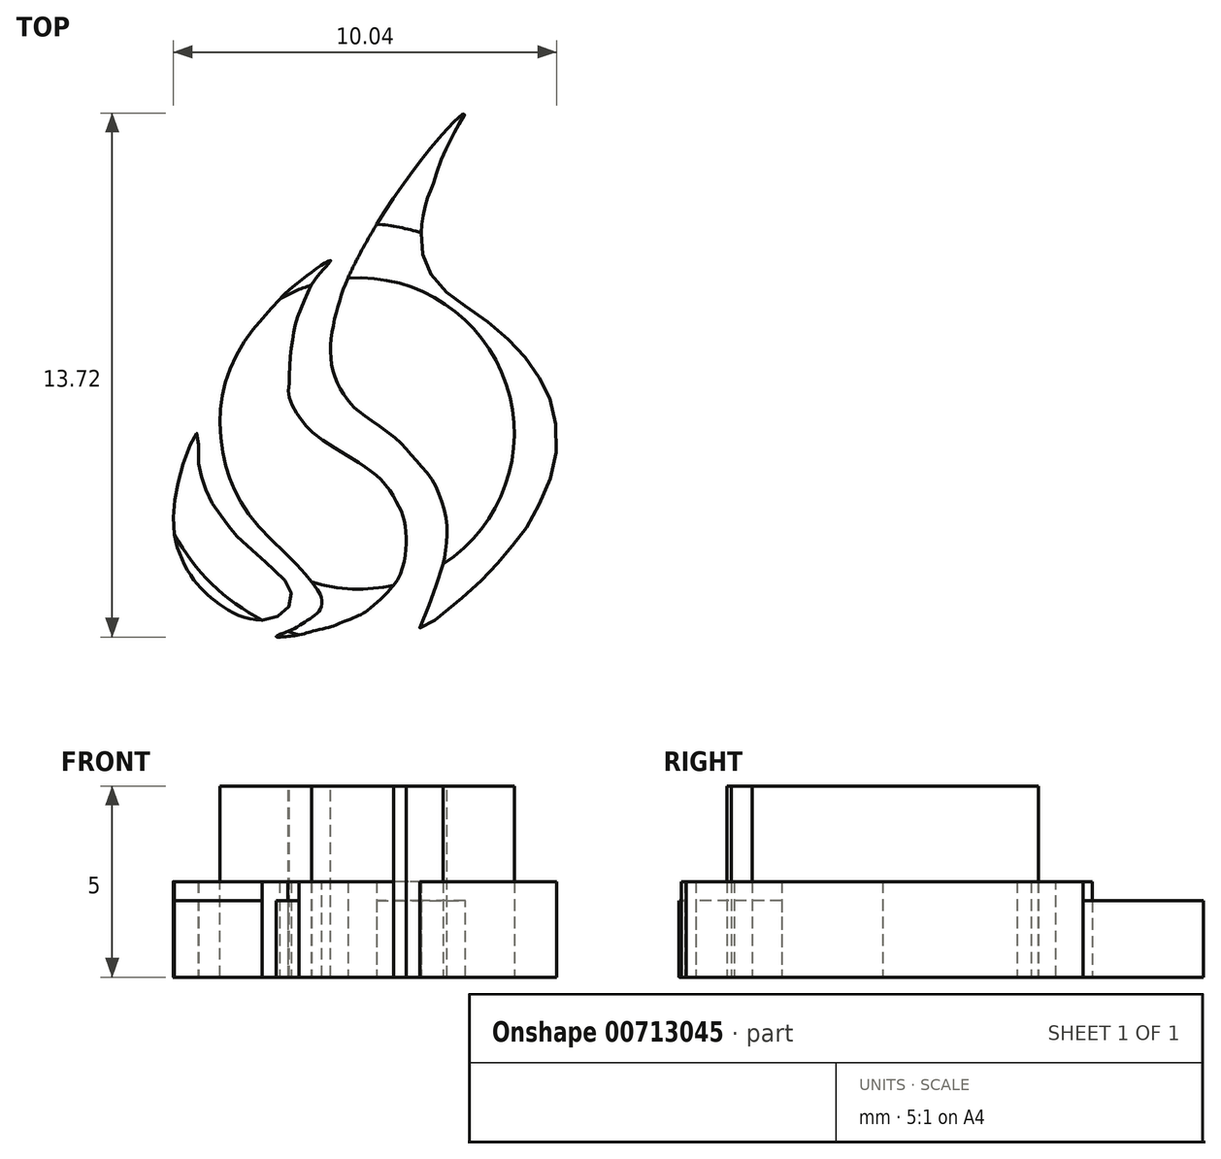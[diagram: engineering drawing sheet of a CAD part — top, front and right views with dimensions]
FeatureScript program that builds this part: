
annotation { "Feature Type Name" : "Feature", "Feature Type Description" : "" }
export const myFeature = defineFeature(function(context is Context, id is Id, definition is map)
    precondition{}
    {
        {
            var Q0;
            Q0=qCreatedBy(makeId("Top.planeOp"),FACE);
            var sketch = newSketch(context, id + "F0", { "sketchPlane" : qUnion([Q0])});
            skCircle(sketch, "E0", {"center": v(0, -0.22) * mm, "radius": 11 * mm});
            skCircle(sketch, "E1", {"center": v(0, -0.22) * mm, "radius": 5.5 * mm});
            skCircle(sketch, "E2", {"center": v(0, -0.22) * mm, "radius": 4.08 * mm});
            skLineSegment(sketch, "E3", {"start": v(0, -7.08) * mm, "end": v(0, -7.71) * mm});
            skLineSegment(sketch, "E4", {"start": v(0, 12.42) * mm, "end": v(0, -12.4) * mm});
            skFitSpline(sketch, "E5", {"points": [v(2.8, 8.17) * mm, v(2.6, 7.83) * mm, v(2.42, 7.47) * mm, v(2.19, 6.99) * mm, v(1.95, 6.3) * mm, v(1.85, 6.06) * mm, v(1.74, 5.7) * mm, v(1.66, 5.3) * mm, v(1.65, 4.93) * mm, v(1.7, 4.4) * mm, v(1.89, 3.95) * mm, v(2.3, 3.48) * mm, v(2.75, 3.15) * mm, v(3.41, 2.68) * mm, v(4, 2.17) * mm, v(4.43, 1.68) * mm, v(4.8, 1.12) * mm, v(5.05, 0.58) * mm, v(5.18, -0.22) * mm, v(5.12, -1.05) * mm, v(4.86, -1.8) * mm, v(4.5, -2.54) * mm, v(4.13, -3.03) * mm, v(3.77, -3.45) * mm, v(3.35, -3.93) * mm, v(2.94, -4.32) * mm, v(1.99, -5.12) * mm, v(1.6, -5.35) * mm, v(1.8, -4.83) * mm, v(1.94, -4.44) * mm, v(2.15, -3.86) * mm, v(2.27, -3.37) * mm, v(2.32, -2.7) * mm, v(2.17, -1.97) * mm, v(1.88, -1.37) * mm, v(1.44, -0.84) * mm, v(1, -0.37) * mm, v(0.26, 0.17) * mm, v(-0.24, 0.6) * mm, v(-0.64, 1.34) * mm, v(-0.72, 2.21) * mm, v(-0.54, 3.1) * mm, v(-0.28, 3.85) * mm, v(0.2, 4.8) * mm, v(0.8, 5.77) * mm, v(1.4, 6.62) * mm, v(2.32, 7.76) * mm, v(2.8, 8.17) * mm]});
            skFitSpline(sketch, "E6", {"points": [v(-0.73, 4.3) * mm, v(-1.1, 3.85) * mm, v(-1.34, 3.44) * mm, v(-1.52, 3.04) * mm, v(-1.66, 2.62) * mm, v(-1.72, 2.32) * mm, v(-1.77, 1.94) * mm, v(-1.8, 1.48) * mm, v(-1.82, 1.06) * mm, v(-1.83, 0.8) * mm, v(-1.7, 0.43) * mm, v(-1.47, 0.1) * mm, v(-1.17, -0.22) * mm, v(-0.24, -0.84) * mm, v(0.4, -1.26) * mm, v(0.82, -1.71) * mm, v(1.08, -2.17) * mm, v(1.2, -2.49) * mm, v(1.24, -2.93) * mm, v(1.22, -3.37) * mm, v(1.08, -3.93) * mm, v(0.8, -4.32) * mm, v(0.58, -4.55) * mm, v(0.27, -4.82) * mm, v(0, -4.99) * mm, v(-0.45, -5.17) * mm, v(-0.72, -5.28) * mm, v(-1.24, -5.4) * mm, v(-1.56, -5.5) * mm, v(-2.16, -5.54) * mm, v(-1.85, -5.4) * mm, v(-1.49, -5.21) * mm, v(-1.2, -5.02) * mm, v(-1, -4.8) * mm, v(-0.98, -4.48) * mm, v(-1.16, -4.19) * mm, v(-1.51, -3.76) * mm, v(-2.61, -2.65) * mm, v(-3.23, -1.72) * mm, v(-3.51, -0.91) * mm, v(-3.63, 0.18) * mm, v(-3.49, 1.1) * mm, v(-3.02, 2.15) * mm, v(-2.33, 3) * mm, v(-1.65, 3.68) * mm, v(-0.73, 4.3) * mm]});
            skFitSpline(sketch, "E7", {"points": [v(-4.22, -0.22) * mm, v(-4.5, -0.77) * mm, v(-4.77, -1.76) * mm, v(-4.85, -2.6) * mm, v(-4.66, -3.42) * mm, v(-4.32, -4.05) * mm, v(-3.98, -4.42) * mm, v(-3.57, -4.73) * mm, v(-3, -5.03) * mm, v(-2.28, -5.07) * mm, v(-1.8, -4.7) * mm, v(-1.84, -4.18) * mm, v(-2.25, -3.77) * mm, v(-2.53, -3.5) * mm, v(-2.85, -3.2) * mm, v(-3.24, -2.84) * mm, v(-3.52, -2.47) * mm, v(-3.87, -1.97) * mm, v(-4.1, -1.43) * mm, v(-4.2, -0.9) * mm, v(-4.22, -0.22) * mm]});
            skSolve(sketch);
        }
        {
            var Q0;
            {var subQ0=sQuery(id+"F0.wireOp",EDGE,"E5");var subQ1=sQuery(id+"F0.wireOp",EDGE,"E1");var subQ2=makeQuery(id+"F0.imprint","INTERSECT",VERTEX,{"disambiguationData":[OD(0.0)],"derivedFrom":[subQ1,subQ0]});Q0=makeQuery(id+"F0.imprint","IMPRINT",FACE,{"disambiguationData":[TD([[makeQuery(id+"F0.imprint","IMPRINT",EDGE,{"disambiguationData":[TD([[subQ2,1.0]])],"derivedFrom":subQ1}),-1.0]])]});}
            var Q1;
            {var subQ0=sQuery(id+"F0.wireOp",EDGE,"E7");var subQ1=sQuery(id+"F0.wireOp",EDGE,"E1");var subQ2=makeQuery(id+"F0.imprint","INTERSECT",VERTEX,{"disambiguationData":[OD(0.0)],"derivedFrom":[subQ1,subQ0]});Q1=makeQuery(id+"F0.imprint","IMPRINT",FACE,{"disambiguationData":[TD([[makeQuery(id+"F0.imprint","IMPRINT",EDGE,{"disambiguationData":[TD([[subQ2,-1.0]])],"derivedFrom":subQ1}),-1.0]])]});}
            var Q2;
            {var subQ0=sQuery(id+"F0.wireOp",EDGE,"E6");var subQ1=sQuery(id+"F0.wireOp",EDGE,"E1");var subQ2=makeQuery(id+"F0.imprint","INTERSECT",VERTEX,{"disambiguationData":[OD(0.0)],"derivedFrom":[subQ1,subQ0]});Q2=makeQuery(id+"F0.imprint","IMPRINT",FACE,{"disambiguationData":[TD([[makeQuery(id+"F0.imprint","IMPRINT",EDGE,{"disambiguationData":[TD([[subQ2,-1.0]])],"derivedFrom":subQ1}),-1.0]])]});}
            extrude(context, id + "F1", {"entities" : qUnion([Q0, Q1, Q2]), "depth" : 2 * mm, "offsetDistance" : 25 * mm});
        }
        {
            var Q0;
            {var subQ0=sQuery(id+"F0.wireOp",EDGE,"E7");var subQ1=sQuery(id+"F0.wireOp",EDGE,"E1");var subQ2=makeQuery(id+"F0.imprint","INTERSECT",VERTEX,{"disambiguationData":[OD(0.0)],"derivedFrom":[subQ1,subQ0]});Q0=makeQuery(id+"F0.imprint","IMPRINT",FACE,{"disambiguationData":[TD([[makeQuery(id+"F0.imprint","IMPRINT",EDGE,{"disambiguationData":[TD([[subQ2,-1.0]])],"derivedFrom":subQ1}),1.0]])]});}
            var Q1;
            {var subQ0=sQuery(id+"F0.wireOp",EDGE,"E6");var subQ1=sQuery(id+"F0.wireOp",EDGE,"E1");var subQ8=makeQuery(id+"F0.imprint","INTERSECT",VERTEX,{"disambiguationData":[OD(0.0)],"derivedFrom":[subQ1,subQ0]});Q1=makeQuery(id+"F0.imprint","IMPRINT",FACE,{"disambiguationData":[TD([[makeQuery(id+"F0.imprint","IMPRINT",EDGE,{"disambiguationData":[TD([[subQ8,-1.0]])],"derivedFrom":subQ1}),1.0]])]});}
            var Q2;
            {var subQ0=sQuery(id+"F0.wireOp",EDGE,"E4");var subQ1=sQuery(id+"F0.wireOp",EDGE,"E2");var subQ2=makeQuery(id+"F0.imprint","INTERSECT",VERTEX,{"disambiguationData":[OD(1.0)],"derivedFrom":[subQ1,subQ0]});Q2=makeQuery(id+"F0.imprint","IMPRINT",FACE,{"disambiguationData":[TD([[makeQuery(id+"F0.imprint","IMPRINT",EDGE,{"disambiguationData":[TD([[subQ2,-1.0]])],"derivedFrom":subQ1}),-1.0]])]});}
            var Q3;
            {var subQ0=sQuery(id+"F0.wireOp",EDGE,"E5");var subQ1=sQuery(id+"F0.wireOp",EDGE,"E1");var subQ8=makeQuery(id+"F0.imprint","INTERSECT",VERTEX,{"disambiguationData":[OD(0.0)],"derivedFrom":[subQ1,subQ0]});Q3=makeQuery(id+"F0.imprint","IMPRINT",FACE,{"disambiguationData":[TD([[makeQuery(id+"F0.imprint","IMPRINT",EDGE,{"disambiguationData":[TD([[subQ8,1.0]])],"derivedFrom":subQ1}),1.0]])]});}
            var Q4;
            {var subQ0=sQuery(id+"F0.wireOp",EDGE,"E6");var subQ1=sQuery(id+"F0.wireOp",EDGE,"E2");var subQ2=makeQuery(id+"F0.imprint","INTERSECT",VERTEX,{"disambiguationData":[OD(0.0)],"derivedFrom":[subQ1,subQ0]});Q4=makeQuery(id+"F0.imprint","IMPRINT",FACE,{"disambiguationData":[TD([[makeQuery(id+"F0.imprint","IMPRINT",EDGE,{"disambiguationData":[TD([[subQ2,-1.0]])],"derivedFrom":subQ1}),-1.0]])]});}
            var Q5;
            {var subQ0=sQuery(id+"F0.wireOp",EDGE,"E5");var subQ1=sQuery(id+"F0.wireOp",EDGE,"E2");var subQ2=makeQuery(id+"F0.imprint","INTERSECT",VERTEX,{"disambiguationData":[OD(0.0)],"derivedFrom":[subQ1,subQ0]});Q5=makeQuery(id+"F0.imprint","IMPRINT",FACE,{"disambiguationData":[TD([[makeQuery(id+"F0.imprint","IMPRINT",EDGE,{"disambiguationData":[TD([[subQ2,1.0]])],"derivedFrom":subQ1}),-1.0]])]});}
            extrude(context, id + "F2", {"entities" : qUnion([Q0, Q1, Q2, Q3, Q4, Q5]), "depth" : 2.5 * mm, "offsetDistance" : 25 * mm});
        }
        {
            var Q0;
            {var subQ0=sQuery(id+"F0.wireOp",EDGE,"E6");var subQ1=sQuery(id+"F0.wireOp",EDGE,"E2");var subQ2=makeQuery(id+"F0.imprint","INTERSECT",VERTEX,{"disambiguationData":[OD(0.0)],"derivedFrom":[subQ1,subQ0]});Q0=makeQuery(id+"F0.imprint","IMPRINT",FACE,{"disambiguationData":[TD([[makeQuery(id+"F0.imprint","IMPRINT",EDGE,{"disambiguationData":[TD([[subQ2,-1.0]])],"derivedFrom":subQ1}),1.0]])]});}
            var Q1;
            {var subQ0=sQuery(id+"F0.wireOp",EDGE,"E4");var subQ1=sQuery(id+"F0.wireOp",EDGE,"E2");var subQ2=makeQuery(id+"F0.imprint","INTERSECT",VERTEX,{"disambiguationData":[OD(1.0)],"derivedFrom":[subQ1,subQ0]});Q1=makeQuery(id+"F0.imprint","IMPRINT",FACE,{"disambiguationData":[TD([[makeQuery(id+"F0.imprint","IMPRINT",EDGE,{"disambiguationData":[TD([[subQ2,-1.0]])],"derivedFrom":subQ1}),1.0]])]});}
            var Q2;
            {var subQ0=sQuery(id+"F0.wireOp",EDGE,"E4");var subQ1=sQuery(id+"F0.wireOp",EDGE,"E2");var subQ2=makeQuery(id+"F0.imprint","INTERSECT",VERTEX,{"disambiguationData":[OD(0.0)],"derivedFrom":[subQ1,subQ0]});Q2=makeQuery(id+"F0.imprint","IMPRINT",FACE,{"disambiguationData":[TD([[makeQuery(id+"F0.imprint","IMPRINT",EDGE,{"disambiguationData":[TD([[subQ2,1.0]])],"derivedFrom":subQ1}),1.0]])]});}
            var Q3;
            {var subQ0=sQuery(id+"F0.wireOp",EDGE,"E5");var subQ1=sQuery(id+"F0.wireOp",EDGE,"E2");var subQ2=makeQuery(id+"F0.imprint","INTERSECT",VERTEX,{"disambiguationData":[OD(0.0)],"derivedFrom":[subQ1,subQ0]});Q3=makeQuery(id+"F0.imprint","IMPRINT",FACE,{"disambiguationData":[TD([[makeQuery(id+"F0.imprint","IMPRINT",EDGE,{"disambiguationData":[TD([[subQ2,1.0]])],"derivedFrom":subQ1}),1.0]])]});}
            extrude(context, id + "F3", {"entities" : qUnion([Q0, Q1, Q2, Q3]), "depth" : 5 * mm, "offsetDistance" : 25 * mm});
        }
    });
